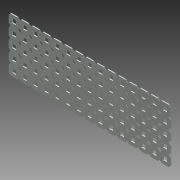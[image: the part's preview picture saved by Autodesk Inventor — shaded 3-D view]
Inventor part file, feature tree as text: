
AUTODESK INVENTOR PART (.ipt)
format: ipt  version: 2013 (Build 170138000, 138)  size: 788,480 bytes
history: native  units: mm (DEFAULTED — no unit token found)
features: other x76, extrude x75, pattern_linear x3, sketch x2, sheet_metal_op x1
ambient origin geometry x8: Origin, YZ Plane, XZ Plane, XY Plane, X Axis, Y Axis, Z Axis, Center Point
bodies: Solid1 (feature_tree)
feature tree (157):
  sheet_metal_op  "Face1"
  pattern_linear  "Rectangular Pattern1"  Spacing1=2.280986mm  [1 undecoded]
  pattern_linear  "Rectangular Pattern2"  Spacing1=2.280986mm  [1 undecoded]
  pattern_linear  "Rectangular Pattern3"  Spacing1=2.280986mm  [1 undecoded]
  sketch  "Sketch1"  dims[d0=12.7mm]
  other  "Plate1"
  sketch  "Sketch2"  dims[d1=12.7mm d2=2.280986mm d3=2.280986mm d4=2.280986mm d5=2.280986mm d6=2.280986mm d7=2.280986mm d8=2.280986mm d9=2.280986mm d10=4.572mm d11=4.572mm d12=4.064mm d13=4.064mm d14=1.1684mm d15=150.0mm d17=12.7mm d18=50.0mm d20=12.7mm d21=25.4mm d22=0.0mm d23=150.0mm d25=12.7mm d26=50.0mm d28=12.7mm d29=0.0mm d30=0.0mm d31=0.0mm d32=0.0mm d33=0.0mm d34=0.0mm d35=0.0mm d36=0.0mm d37=0.0mm d38=0.0mm d39=0.0mm d40=0.0mm d41=0.0mm d42=0.0mm d43=0.0mm d44=0.0mm d45=0.0mm d46=0.0mm d47=0.0mm d48=0.0mm d49=0.0mm d50=0.0mm d51=0.0mm d52=0.0mm d53=0.0mm d54=0.0mm d55=0.0mm d56=0.0mm d57=0.0mm d58=0.0mm d59=0.0mm d60=0.0mm d61=0.0mm d62=0.0mm d63=0.0mm d64=0.0mm d65=0.0mm d66=0.0mm d67=0.0mm d68=0.0mm d69=0.0mm d70=0.0mm d71=0.0mm d72=0.0mm d73=0.0mm d74=0.0mm d75=0.0mm d76=0.0mm d77=0.0mm d78=0.0mm d79=0.0mm d80=0.0mm d81=0.0mm d82=0.0mm d83=0.0mm d84=0.0mm d85=0.0mm d86=0.0mm d87=0.0mm d88=0.0mm d89=0.0mm d90=0.0mm d91=0.0mm d92=0.0mm d93=0.0mm d94=0.0mm d95=0.0mm d96=0.0mm d97=0.0mm d98=0.0mm d99=0.0mm d100=0.0mm d101=0.0mm d102=0.0mm d103=0.0mm d104=0.0mm d105=0.0mm d106=0.0mm d107=0.0mm d108=0.0mm d109=0.0mm d110=0.0mm d111=0.0mm d112=0.0mm d113=0.0mm d114=0.0mm d115=0.0mm d116=0.0mm d117=0.0mm d118=0.0mm d119=0.0mm d120=0.0mm d121=0.0mm d122=0.0mm d123=0.0mm d124=0.0mm d125=0.0mm d126=0.0mm d127=0.0mm d128=0.0mm d129=0.0mm d130=0.0mm d131=0.0mm d132=0.0mm d133=0.0mm d134=0.0mm d135=0.0mm d136=0.0mm d137=0.0mm d138=0.0mm d139=0.0mm d140=0.0mm d141=0.0mm d142=0.0mm d143=0.0mm d144=0.0mm d145=0.0mm d146=0.0mm d147=0.0mm d148=0.0mm d149=0.0mm d150=0.0mm d151=0.0mm d152=0.0mm d153=0.0mm d154=0.0mm d155=0.0mm d156=0.0mm d157=0.0mm d158=0.0mm d159=0.0mm d160=0.0mm d161=0.0mm d162=0.0mm d163=0.0mm d164=0.0mm d165=0.0mm d166=0.0mm d167=0.0mm d168=0.0mm d169=0.0mm d170=0.0mm d171=0.0mm d172=0.0mm d173=0.0mm d174=0.0mm d175=0.0mm d176=0.0mm d177=0.0mm d178=0.0mm]
  other  "Srf1"
  other  "Srf2"
  other  "Srf3"
  other  "Srf4"
  other  "Srf5"
  other  "Srf6"
  other  "Srf7"
  other  "Srf8"
  other  "Srf9"
  other  "Srf10"
  other  "Srf11"
  other  "Srf12"
  other  "Srf13"
  other  "Srf14"
  other  "Srf15"
  other  "Srf16"
  other  "Srf17"
  other  "Srf18"
  other  "Srf19"
  other  "Srf20"
  other  "Srf21"
  other  "Srf22"
  other  "Srf23"
  other  "Srf24"
  other  "Srf25"
  other  "Srf26"
  other  "Srf27"
  other  "Srf28"
  other  "Srf29"
  other  "Srf30"
  other  "Srf31"
  other  "Srf32"
  other  "Srf33"
  other  "Srf34"
  other  "Srf35"
  other  "Srf36"
  other  "Srf37"
  other  "Srf38"
  other  "Srf39"
  other  "Srf40"
  other  "Srf41"
  other  "Srf42"
  other  "Srf43"
  other  "Srf44"
  other  "Srf45"
  other  "Srf46"
  other  "Srf47"
  other  "Srf48"
  other  "Srf49"
  other  "Srf50"
  other  "Srf51"
  other  "Srf52"
  other  "Srf53"
  other  "Srf54"
  other  "Srf55"
  other  "Srf56"
  other  "Srf57"
  other  "Srf58"
  other  "Srf59"
  other  "Srf60"
  other  "Srf61"
  other  "Srf62"
  other  "Srf63"
  other  "Srf64"
  other  "Srf65"
  other  "Srf66"
  other  "Srf67"
  other  "Srf68"
  other  "Srf69"
  other  "Srf70"
  other  "Srf71"
  other  "Srf72"
  other  "Srf73"
  other  "Srf74"
  other  "Srf75"
  extrude  "ExtrusionSrf1"  Depth=2.280986mm
  extrude  "ExtrusionSrf2"  Depth=2.280986mm
  extrude  "ExtrusionSrf3"  Depth=2.280986mm
  extrude  "ExtrusionSrf4"  Depth=2.280986mm
  extrude  "ExtrusionSrf5"  Depth=2.280986mm
  extrude  "ExtrusionSrf6"  Depth=4.572mm
  extrude  "ExtrusionSrf7"  Depth=4.572mm
  extrude  "ExtrusionSrf8"  Depth=4.064mm
  extrude  "ExtrusionSrf9"  Depth=4.064mm
  extrude  "ExtrusionSrf10"  Depth=1.1684mm
  extrude  "ExtrusionSrf11"  Depth=150.0mm
  extrude  "ExtrusionSrf12"  Depth=50.0mm
  extrude  "ExtrusionSrf13"  Depth=25.4mm TaperAngle=0.0deg
  extrude  "ExtrusionSrf14"  Depth=150.0mm
  extrude  "ExtrusionSrf15"  Depth=50.0mm
  extrude  "ExtrusionSrf16"  TaperAngle=0.0deg  [1 undecoded]
  extrude  "ExtrusionSrf17"  TaperAngle=0.0deg  [1 undecoded]
  extrude  "ExtrusionSrf18"  TaperAngle=0.0deg  [1 undecoded]
  extrude  "ExtrusionSrf19"  TaperAngle=0.0deg  [1 undecoded]
  extrude  "ExtrusionSrf20"  TaperAngle=0.0deg  [1 undecoded]
  extrude  "ExtrusionSrf21"  TaperAngle=0.0deg  [1 undecoded]
  extrude  "ExtrusionSrf22"  TaperAngle=0.0deg  [1 undecoded]
  extrude  "ExtrusionSrf23"  TaperAngle=0.0deg  [1 undecoded]
  extrude  "ExtrusionSrf24"  TaperAngle=0.0deg  [1 undecoded]
  extrude  "ExtrusionSrf25"  TaperAngle=0.0deg  [1 undecoded]
  extrude  "ExtrusionSrf26"  TaperAngle=0.0deg  [1 undecoded]
  extrude  "ExtrusionSrf27"  TaperAngle=0.0deg  [1 undecoded]
  extrude  "ExtrusionSrf28"  TaperAngle=0.0deg  [1 undecoded]
  extrude  "ExtrusionSrf29"  TaperAngle=0.0deg  [1 undecoded]
  extrude  "ExtrusionSrf30"  TaperAngle=0.0deg  [1 undecoded]
  extrude  "ExtrusionSrf31"  TaperAngle=0.0deg  [1 undecoded]
  extrude  "ExtrusionSrf32"  TaperAngle=0.0deg  [1 undecoded]
  extrude  "ExtrusionSrf33"  TaperAngle=0.0deg  [1 undecoded]
  extrude  "ExtrusionSrf34"  TaperAngle=0.0deg  [1 undecoded]
  extrude  "ExtrusionSrf35"  TaperAngle=0.0deg  [1 undecoded]
  extrude  "ExtrusionSrf36"  TaperAngle=0.0deg  [1 undecoded]
  extrude  "ExtrusionSrf37"  TaperAngle=0.0deg  [1 undecoded]
  extrude  "ExtrusionSrf38"  TaperAngle=0.0deg  [1 undecoded]
  extrude  "ExtrusionSrf39"  TaperAngle=0.0deg  [1 undecoded]
  extrude  "ExtrusionSrf40"  TaperAngle=0.0deg  [1 undecoded]
  extrude  "ExtrusionSrf41"  TaperAngle=0.0deg  [1 undecoded]
  extrude  "ExtrusionSrf42"  TaperAngle=0.0deg  [1 undecoded]
  extrude  "ExtrusionSrf43"  TaperAngle=0.0deg  [1 undecoded]
  extrude  "ExtrusionSrf44"  TaperAngle=0.0deg  [1 undecoded]
  extrude  "ExtrusionSrf45"  TaperAngle=0.0deg  [1 undecoded]
  extrude  "ExtrusionSrf46"  TaperAngle=0.0deg  [1 undecoded]
  extrude  "ExtrusionSrf47"  TaperAngle=0.0deg  [1 undecoded]
  extrude  "ExtrusionSrf48"  TaperAngle=0.0deg  [1 undecoded]
  extrude  "ExtrusionSrf49"  TaperAngle=0.0deg  [1 undecoded]
  extrude  "ExtrusionSrf50"  TaperAngle=0.0deg  [1 undecoded]
  extrude  "ExtrusionSrf51"  TaperAngle=0.0deg  [1 undecoded]
  extrude  "ExtrusionSrf52"  TaperAngle=0.0deg  [1 undecoded]
  extrude  "ExtrusionSrf53"  TaperAngle=0.0deg  [1 undecoded]
  extrude  "ExtrusionSrf54"  TaperAngle=0.0deg  [1 undecoded]
  extrude  "ExtrusionSrf55"  TaperAngle=0.0deg  [1 undecoded]
  extrude  "ExtrusionSrf56"  TaperAngle=0.0deg  [1 undecoded]
  extrude  "ExtrusionSrf57"  TaperAngle=0.0deg  [1 undecoded]
  extrude  "ExtrusionSrf58"  TaperAngle=0.0deg  [1 undecoded]
  extrude  "ExtrusionSrf59"  TaperAngle=0.0deg  [1 undecoded]
  extrude  "ExtrusionSrf60"  TaperAngle=0.0deg  [1 undecoded]
  extrude  "ExtrusionSrf61"  TaperAngle=0.0deg  [1 undecoded]
  extrude  "ExtrusionSrf62"  TaperAngle=0.0deg  [1 undecoded]
  extrude  "ExtrusionSrf63"  TaperAngle=0.0deg  [1 undecoded]
  extrude  "ExtrusionSrf64"  TaperAngle=0.0deg  [1 undecoded]
  extrude  "ExtrusionSrf65"  TaperAngle=0.0deg  [1 undecoded]
  extrude  "ExtrusionSrf66"  TaperAngle=0.0deg  [1 undecoded]
  extrude  "ExtrusionSrf67"  TaperAngle=0.0deg  [1 undecoded]
  extrude  "ExtrusionSrf68"  TaperAngle=0.0deg  [1 undecoded]
  extrude  "ExtrusionSrf69"  TaperAngle=0.0deg  [1 undecoded]
  extrude  "ExtrusionSrf70"  TaperAngle=0.0deg  [1 undecoded]
  extrude  "ExtrusionSrf71"  TaperAngle=0.0deg  [1 undecoded]
  extrude  "ExtrusionSrf72"  TaperAngle=0.0deg  [1 undecoded]
  extrude  "ExtrusionSrf73"  TaperAngle=0.0deg  [1 undecoded]
  extrude  "ExtrusionSrf74"  TaperAngle=0.0deg  [1 undecoded]
  extrude  "ExtrusionSrf75"  TaperAngle=0.0deg  [1 undecoded]
note: 63 required parameter values undecoded (feature->parameter linkage not recoverable at this tier; creation-order binding heuristic only, values carry confidence <= 0.55)
